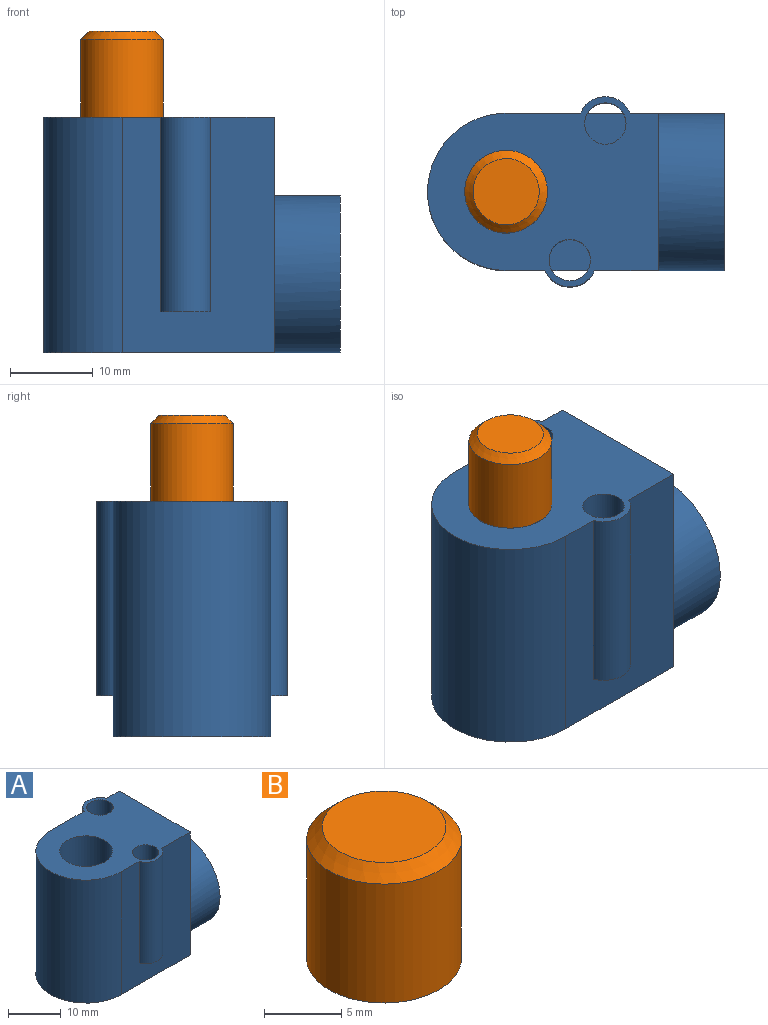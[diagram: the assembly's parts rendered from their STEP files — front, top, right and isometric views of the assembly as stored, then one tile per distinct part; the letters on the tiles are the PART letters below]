
ASSEMBLY  parts=2 mates=1
PART A: 20 faces, bbox 35.9x23x28.5 mm
  f0: plane 9.5x9.5mm, normal (1,0,0), area 19.4mm2, adj f5,f8,f18
  f1: plane 19x19mm, normal (1,0,0), area 219.2mm2, adj f5,f7,f15,f18
  f2: plane 5x3.75mm, normal (0,0,1), area 15.8mm2, adj f5,f13
  f3: plane 5x3.75mm, normal (0,0,1), area 15.8mm2, adj f7,f14
  f4: plane 9.5x9.5mm, normal (1,0,0), area 19.4mm2, adj f7,f8,f18
  f5: plane 28.5x18.4mm, normal (0,1,0), area 383.4mm2, adj f0,f1,f2,f6,f8,f9,f11,f15
  f6: cylinder r=9.5mm len=28.5mm, axis (0,0,1), area 850.6mm2, adj f5,f7,f8,f15
  f7: plane 28.5x18.4mm, normal (0,-1,0), area 383.4mm2, adj f1,f3,f4,f6,f8,f10,f12,f15
  f8: plane 27.9x19mm, normal (0,0,-1), area 491.4mm2, adj f0,f4,f5,f6,f7
  f9: plane 6x2mm, normal (0,0,-1), area 4.8mm2, adj f5,f11,f13
  f10: plane 6x2mm, normal (0,0,-1), area 4.8mm2, adj f7,f12,f14
  f11: cylinder r=3.25mm len=23.5mm, axis (0,0,-1), area 179.6mm2, adj f5,f9,f15
  f12: cylinder r=3.25mm len=23.5mm, axis (0,0,-1), area 179.6mm2, adj f7,f10,f15
  f13: cylinder r=2.5mm len=23.5mm, axis (0,0,-1), area 369.1mm2, adj f2,f9,f15
  f14: cylinder r=2.5mm len=23.5mm, axis (0,0,-1), area 369.1mm2, adj f3,f10,f15
  f15: plane 27.9x23mm, normal (0,0,1), area 390.9mm2, adj f1,f5,f6,f7,f11,f12,f13,f14
  f16: cylinder r=5mm len=16.1mm, axis (0,0,1), area 505.8mm2, adj f15,f17
  f17: plane 10x10mm, normal (0,0,1), area 78.5mm2, adj f16
  f18: cylinder r=9.5mm len=19mm, axis (-1,0,0), area 477.5mm2, adj f0,f1,f4,f19
  f19: plane 19x19mm, normal (1,0,0), area 283.5mm2, adj f18
PART B: 4 faces, bbox 10x10x10.4 mm
  f0: cylinder r=5mm len=10mm, axis (0,0,-1), area 295.3mm2, adj f2,f3
  f1: plane 8x8mm, normal (0,0,1), area 50.3mm2, adj f3
  f2: plane 10x10mm, normal (0,0,-1), area 78.5mm2, adj f0
  f3: cone r=4mm half-angle=45deg, axis (0,0,-1), area 40mm2, adj f0,f1
PLACE A rot(axis=(0,0,1),0deg) t=(11,-11.03,1.57)mm
PLACE B rot(axis=(0,0,-1),180deg) t=(11,-11.03,1.57)mm
MATE slider B.f0 <-> A.f16  axis (0,0,-1) through (11,-11.03,25.07)mm
